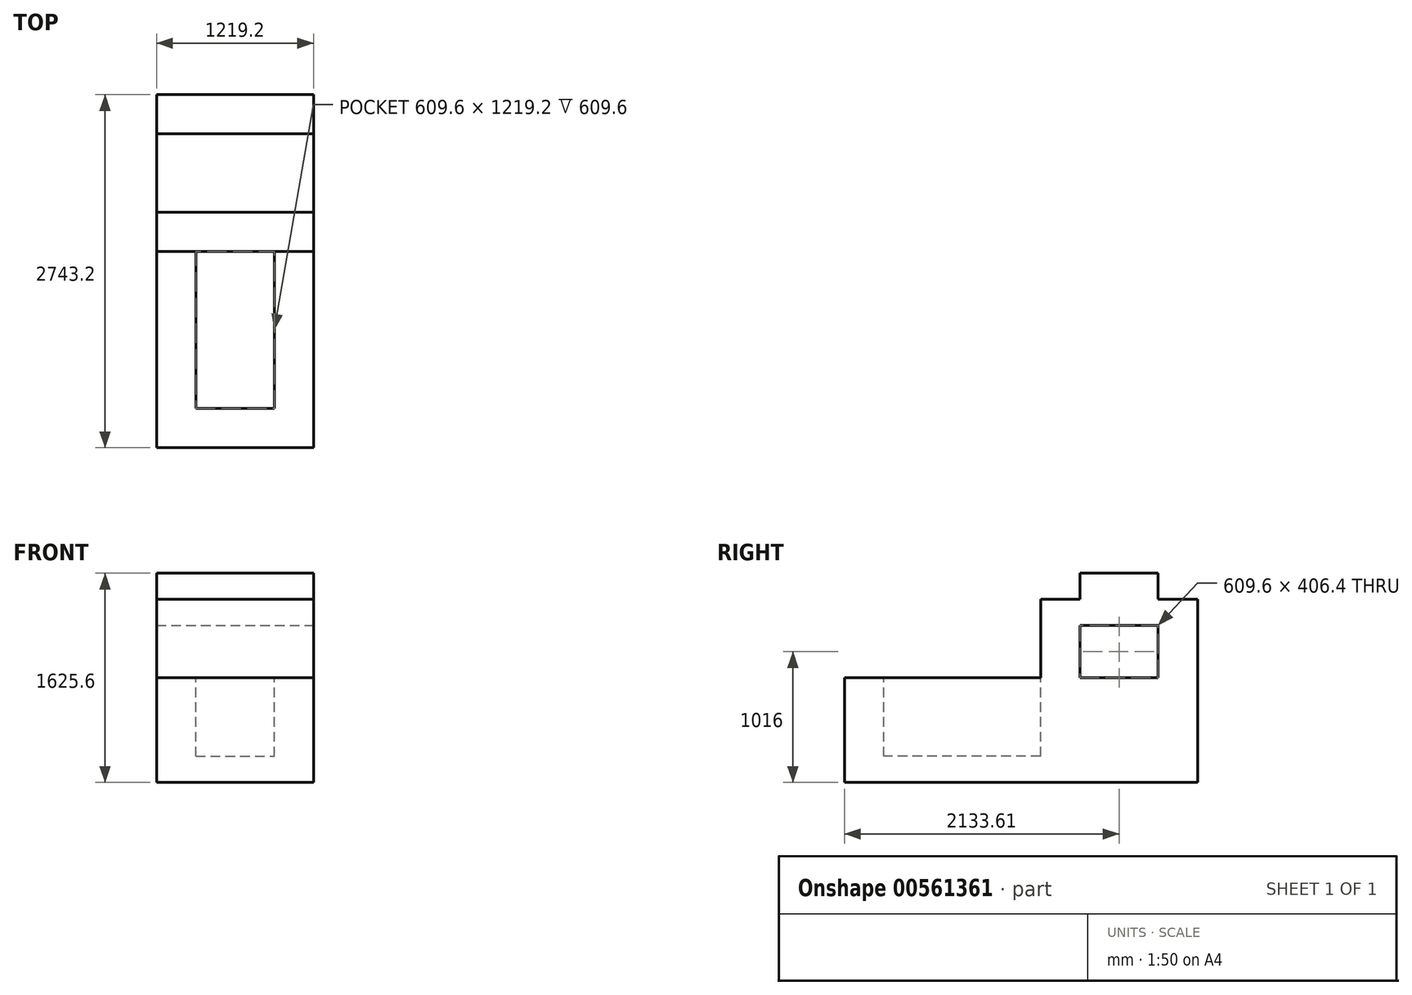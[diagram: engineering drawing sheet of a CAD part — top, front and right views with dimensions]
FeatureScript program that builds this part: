
annotation { "Feature Type Name" : "Feature", "Feature Type Description" : "" }
export const myFeature = defineFeature(function(context is Context, id is Id, definition is map)
    precondition{}
    {
        {
            var Q0;
            Q0=qCreatedBy(makeId("Right.planeOp"),FACE);
            var sketch = newSketch(context, id + "F0", { "sketchPlane" : qUnion([Q0])});
            skLineSegment(sketch, "E0.bottom", {"start": v(-76.1, -75.06) * mm, "end": v(2667.1, -75.06) * mm});
            skLineSegment(sketch, "E0.top", {"start": v(-76.1, 1550.54) * mm, "end": v(2667.1, 1550.54) * mm});
            skLineSegment(sketch, "E0.left", {"start": v(-76.1, -75.06) * mm, "end": v(-76.1, 1550.54) * mm});
            skLineSegment(sketch, "E0.right", {"start": v(2667.1, -75.06) * mm, "end": v(2667.1, 1550.54) * mm});
            skSolve(sketch);
        }
        {
            var Q0;
            Q0 = qSketchRegion(id + "F0", true);
            extrude(context, id + "F1", {"entities" : qUnion([Q0]), "depth" : 1219.2 * mm, "offsetDistance" : 25.4 * mm});
        }
        {
            var Q0;
            Q0=makeQuery(id+"F1.opExtrude","CAP_FACE",FACE,{"disambiguationData":[OSD([sQuery(id+"F0.wireOp",EDGE,"E0.bottom"),sQuery(id+"F0.wireOp",EDGE,"E0.top"),sQuery(id+"F0.wireOp",EDGE,"E0.left"),sQuery(id+"F0.wireOp",EDGE,"E0.right")])],"isStart":false});
            var sketch = newSketch(context, id + "F2", { "sketchPlane" : qUnion([Q0])});
            skLineSegment(sketch, "E1", {"start": v(2667.1, -75.06) * mm, "end": v(2667.1, 737.74) * mm});
            skLineSegment(sketch, "E2", {"start": v(2362.3, 737.74) * mm, "end": v(2362.3, 1144.14) * mm});
            skLineSegment(sketch, "E3", {"start": v(2362.3, 1144.14) * mm, "end": v(1752.7, 1144.14) * mm});
            skLineSegment(sketch, "E4", {"start": v(1752.7, 1144.14) * mm, "end": v(1752.7, 737.74) * mm});
            skLineSegment(sketch, "E5", {"start": v(1752.7, 737.74) * mm, "end": v(2362.3, 737.74) * mm});
            skSolve(sketch);
        }
        {
            var Q0;
            Q0=makeQuery(id+"F2.imprint","IMPRINT",FACE,{"disambiguationData":[TD([[makeQuery(id+"F2.imprint","IMPRINT",EDGE,{"derivedFrom":sQuery(id+"F2.wireOp",EDGE,"E2")}),1.0]])]});
            extrude(context, id + "F3", {"entities" : qUnion([Q0]), "operationType" : NewBodyOperationType.REMOVE, "endBound" : BoundingType.THROUGH_ALL, "oppositeDirection" : true, "depth" : 25.4 * mm, "offsetDistance" : 25.4 * mm});
        }
        {
            var Q0;
            Q0=makeQuery(id+"F1.opExtrude","CAP_FACE",FACE,{"disambiguationData":[OSD([sQuery(id+"F0.wireOp",EDGE,"E0.bottom"),sQuery(id+"F0.wireOp",EDGE,"E0.top"),sQuery(id+"F0.wireOp",EDGE,"E0.left"),sQuery(id+"F0.wireOp",EDGE,"E0.right")])],"isStart":false});
            var sketch = newSketch(context, id + "F4", { "sketchPlane" : qUnion([Q0])});
            skLineSegment(sketch, "E6", {"start": v(2667.1, 1550.54) * mm, "end": v(2667.1, 1347.34) * mm});
            skLineSegment(sketch, "E7", {"start": v(2667.1, 1347.34) * mm, "end": v(2362.3, 1347.34) * mm});
            skLineSegment(sketch, "E8", {"start": v(2362.3, 1347.34) * mm, "end": v(2362.3, 1550.54) * mm});
            skLineSegment(sketch, "E9", {"start": v(2362.3, 1550.54) * mm, "end": v(2362.3, 1347.34) * mm});
            skLineSegment(sketch, "E10", {"start": v(2362.3, 1550.54) * mm, "end": v(1752.7, 1550.54) * mm});
            skLineSegment(sketch, "E11", {"start": v(1752.7, 1550.54) * mm, "end": v(1752.7, 1347.34) * mm});
            skLineSegment(sketch, "E12", {"start": v(1752.7, 1347.34) * mm, "end": v(1447.9, 1347.34) * mm});
            skLineSegment(sketch, "E13", {"start": v(1447.9, 1347.34) * mm, "end": v(1447.9, 1550.54) * mm});
            skLineSegment(sketch, "E14", {"start": v(1447.9, 1550.54) * mm, "end": v(1752.7, 1550.54) * mm});
            skLineSegment(sketch, "E15", {"start": v(2362.3, 1550.54) * mm, "end": v(2667.1, 1550.54) * mm});
            skSolve(sketch);
        }
        {
            var Q0;
            Q0=makeQuery(id+"F4.imprint","IMPRINT",FACE,{"disambiguationData":[TD([[makeQuery(id+"F4.imprint","IMPRINT",EDGE,{"derivedFrom":sQuery(id+"F4.wireOp",EDGE,"E6")}),1.0]])]});
            var Q1;
            Q1=makeQuery(id+"F4.imprint","IMPRINT",FACE,{"disambiguationData":[TD([[makeQuery(id+"F4.imprint","IMPRINT",EDGE,{"derivedFrom":sQuery(id+"F4.wireOp",EDGE,"E11")}),-1.0]])]});
            extrude(context, id + "F5", {"entities" : qUnion([Q0, Q1]), "operationType" : NewBodyOperationType.REMOVE, "endBound" : BoundingType.THROUGH_ALL, "oppositeDirection" : true, "depth" : 25.4 * mm, "offsetDistance" : 25.4 * mm});
        }
        {
            var Q0;
            Q0=makeQuery(id+"F1.opExtrude","CAP_FACE",FACE,{"disambiguationData":[OSD([sQuery(id+"F0.wireOp",EDGE,"E0.bottom"),sQuery(id+"F0.wireOp",EDGE,"E0.top"),sQuery(id+"F0.wireOp",EDGE,"E0.left"),sQuery(id+"F0.wireOp",EDGE,"E0.right")])],"isStart":false});
            var sketch = newSketch(context, id + "F6", { "sketchPlane" : qUnion([Q0])});
            skLineSegment(sketch, "E16", {"start": v(2667.1, -75.06) * mm, "end": v(1447.9, -75.06) * mm});
            skLineSegment(sketch, "E17", {"start": v(1447.9, -75.06) * mm, "end": v(-76.1, -75.06) * mm});
            skLineSegment(sketch, "E18", {"start": v(-76.1, -75.06) * mm, "end": v(-76.1, 737.74) * mm});
            skLineSegment(sketch, "E19", {"start": v(-76.1, 737.74) * mm, "end": v(1447.9, 737.74) * mm});
            skLineSegment(sketch, "E20", {"start": v(1447.9, 737.74) * mm, "end": v(1447.9, 1347.34) * mm});
            skSolve(sketch);
        }
        {
            var Q0;
            {var subQ5=sQuery(id+"F6.wireOp",EDGE,"E19");Q0=makeQuery(id+"F6.imprint","IMPRINT",FACE,{"disambiguationData":[TD([[makeQuery(id+"F6.imprint","IMPRINT",EDGE,{"derivedFrom":subQ5}),1.0]])]});}
            extrude(context, id + "F7", {"entities" : qUnion([Q0]), "operationType" : NewBodyOperationType.REMOVE, "endBound" : BoundingType.THROUGH_ALL, "oppositeDirection" : true, "depth" : 25.4 * mm, "offsetDistance" : 25.4 * mm});
        }
        {
            var Q0;
            Q0=makeQuery(id+"F7.boolean.opBoolean","COPY",FACE,{"derivedFrom":makeQuery(id+"F7.opExtrude","SWEPT_FACE",FACE,{"disambiguationData":[OSD([sQuery(id+"F6.wireOp",EDGE,"E19")])]})});
            var sketch = newSketch(context, id + "F8", { "sketchPlane" : qUnion([Q0])});
            skLineSegment(sketch, "E21", {"start": v(304.8, 1447.9) * mm, "end": v(914.4, 1447.9) * mm});
            skLineSegment(sketch, "E22", {"start": v(914.4, 1447.9) * mm, "end": v(914.4, 228.7) * mm});
            skLineSegment(sketch, "E23", {"start": v(914.4, 228.7) * mm, "end": v(304.8, 228.7) * mm});
            skLineSegment(sketch, "E24", {"start": v(304.8, 1447.9) * mm, "end": v(304.8, 228.7) * mm});
            skSolve(sketch);
        }
        {
            var Q0;
            Q0=makeQuery(id+"F8.imprint","IMPRINT",FACE,{"disambiguationData":[TD([[makeQuery(id+"F8.imprint","IMPRINT",EDGE,{"derivedFrom":sQuery(id+"F8.wireOp",EDGE,"E21")}),-1.0]])]});
            extrude(context, id + "F9", {"entities" : qUnion([Q0]), "operationType" : NewBodyOperationType.REMOVE, "oppositeDirection" : true, "depth" : 609.6 * mm, "offsetDistance" : 25.4 * mm});
        }
    });
